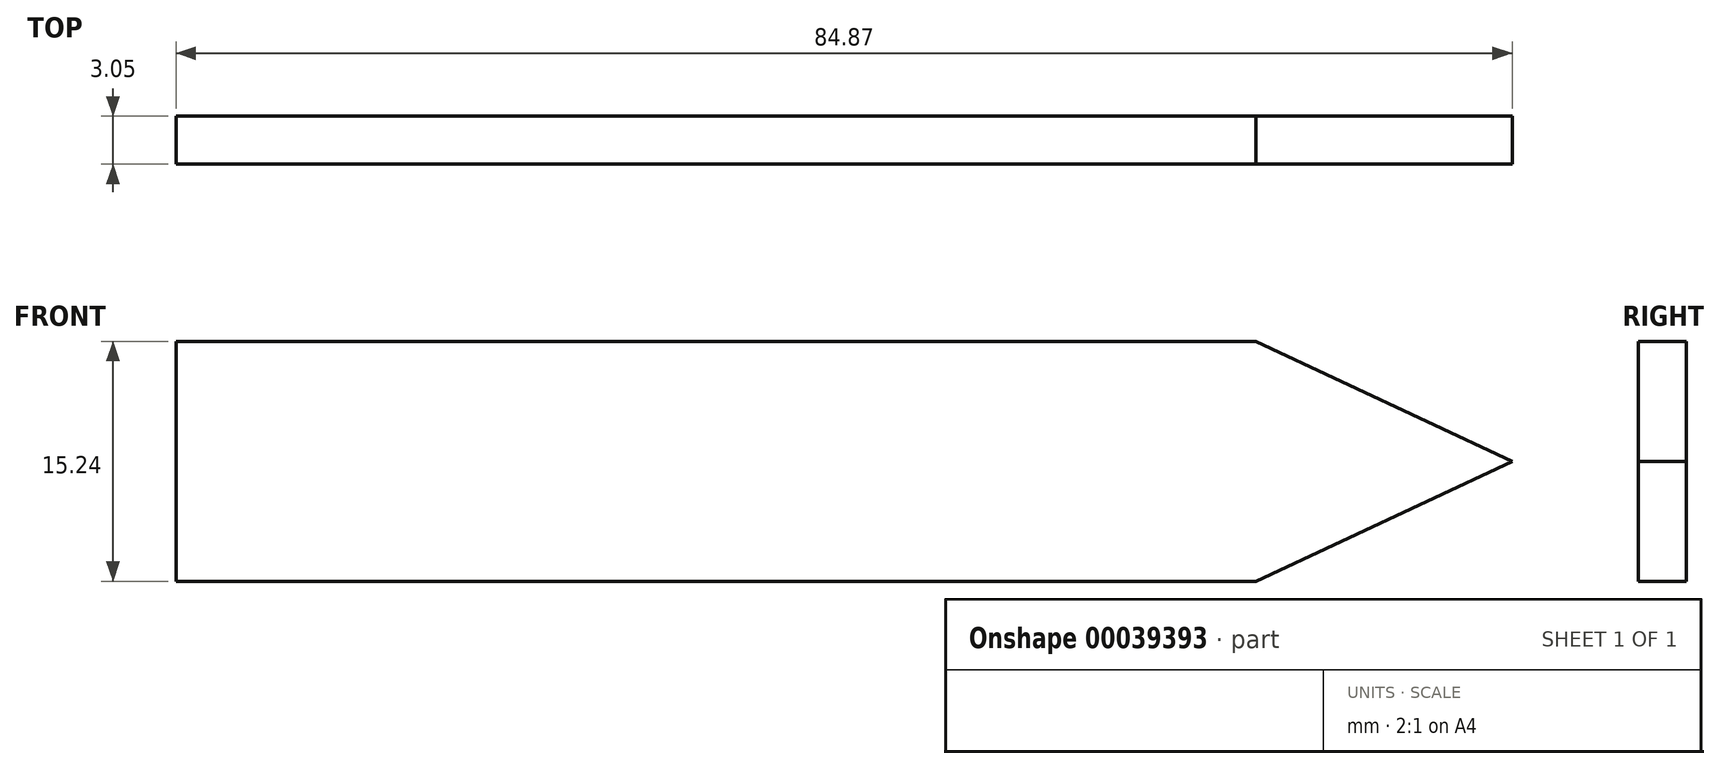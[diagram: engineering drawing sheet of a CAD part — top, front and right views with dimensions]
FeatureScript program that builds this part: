
annotation { "Feature Type Name" : "Feature", "Feature Type Description" : "" }
export const myFeature = defineFeature(function(context is Context, id is Id, definition is map)
    precondition{}
    {
        {
            var Q0;
            Q0=qCreatedBy(makeId("Front.planeOp"),FACE);
            var sketch = newSketch(context, id + "F0", { "sketchPlane" : qUnion([Q0])});
            skLineSegment(sketch, "E0.bottom", {"start": v(0, 0) * mm, "end": v(68.58, 0) * mm});
            skLineSegment(sketch, "E0.top", {"start": v(0, 15.24) * mm, "end": v(68.58, 15.24) * mm});
            skLineSegment(sketch, "E0.left", {"start": v(0, 0) * mm, "end": v(0, 15.24) * mm});
            skLineSegment(sketch, "E0.right", {"start": v(68.58, 0) * mm, "end": v(68.58, 15.24) * mm});
            skLineSegment(sketch, "E1", {"start": v(68.58, 15.24) * mm, "end": v(84.87, 7.62) * mm});
            skPoint(sketch, "E1.endSnap0", {"position": v(68.58, 7.62) * mm});
            skLineSegment(sketch, "E2", {"start": v(84.87, 7.62) * mm, "end": v(68.58, 0) * mm});
            skSolve(sketch);
        }
        {
            var Q0;
            Q0 = qSketchRegion(id + "F0", true);
            extrude(context, id + "F1", {"entities" : qUnion([Q0]), "depth" : 3.05 * mm});
        }
    });
